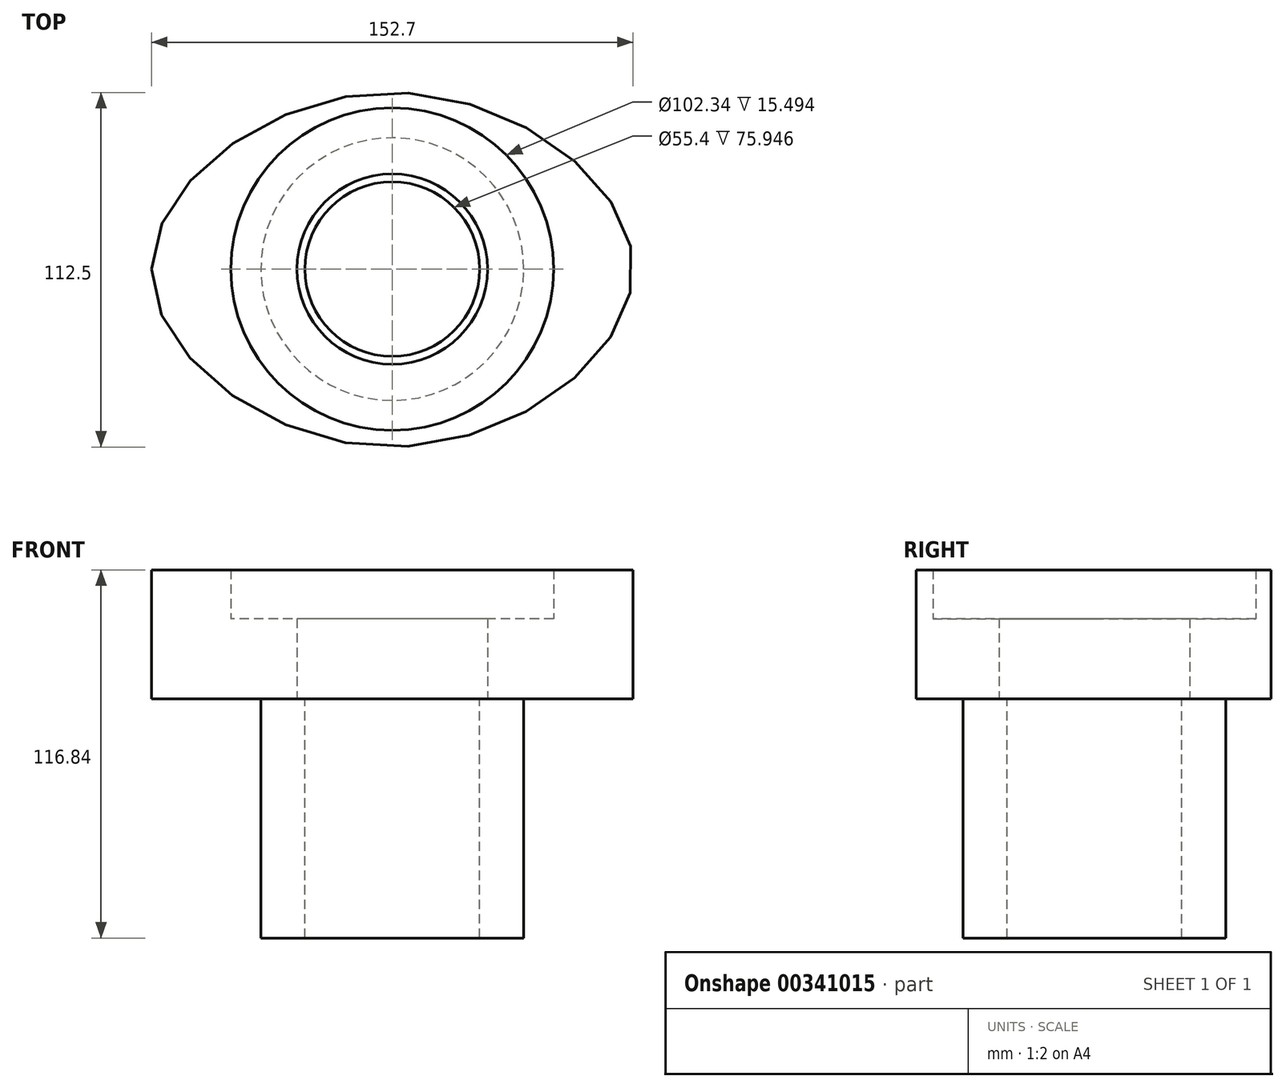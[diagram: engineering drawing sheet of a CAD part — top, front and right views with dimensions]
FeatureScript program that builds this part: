
annotation { "Feature Type Name" : "Feature", "Feature Type Description" : "" }
export const myFeature = defineFeature(function(context is Context, id is Id, definition is map)
    precondition{}
    {
        {
            var Q0;
            Q0=qCreatedBy(makeId("Top.planeOp"),FACE);
            var sketch = newSketch(context, id + "F0", { "sketchPlane" : qUnion([Q0])});
            skCircle(sketch, "E0", {"center": v(0, 0) * mm, "radius": 30.2 * mm});
            skCircle(sketch, "E1", {"center": v(0, 0) * mm, "radius": 51.17 * mm});
            skFitSpline(sketch, "E2", {"points": [v(-76.35, 0) * mm, v(0, 56.05) * mm, v(76.35, 0) * mm, v(0, -56.45) * mm, v(-76.35, 0) * mm]});
            skSolve(sketch);
        }
        {
            var Q0;
            Q0=makeQuery(id+"F0.imprint","IMPRINT",FACE,{"disambiguationData":[TD([[makeQuery(id+"F0.imprint","IMPRINT",EDGE,{"derivedFrom":sQuery(id+"F0.wireOp",EDGE,"E0")}),-1.0]])]});
            extrude(context, id + "F1", {"entities" : qUnion([Q0]), "depth" : 25.4 * mm});
        }
        {
            var Q0;
            Q0=makeQuery(id+"F0.imprint","IMPRINT",FACE,{"disambiguationData":[TD([[makeQuery(id+"F0.imprint","IMPRINT",EDGE,{"derivedFrom":sQuery(id+"F0.wireOp",EDGE,"E1")}),-1.0]])]});
            extrude(context, id + "F2", {"entities" : qUnion([Q0]), "operationType" : NewBodyOperationType.ADD, "depth" : 40.9 * mm});
        }
        {
            var Q0;
            Q0=qCreatedBy(makeId("Top.planeOp"),FACE);
            var sketch = newSketch(context, id + "F3", { "sketchPlane" : qUnion([Q0])});
            skCircle(sketch, "E3", {"center": v(0, 0) * mm, "radius": 41.68 * mm});
            skCircle(sketch, "E4", {"center": v(0, 0) * mm, "radius": 27.7 * mm});
            skSolve(sketch);
        }
        {
            var Q0;
            Q0=makeQuery(id+"F3.imprint","IMPRINT",FACE,{"disambiguationData":[TD([[makeQuery(id+"F3.imprint","IMPRINT",EDGE,{"derivedFrom":sQuery(id+"F3.wireOp",EDGE,"E3")}),1.0]])]});
            extrude(context, id + "F4", {"entities" : qUnion([Q0]), "operationType" : NewBodyOperationType.ADD, "oppositeDirection" : true, "depth" : 75.95 * mm});
        }
    });
